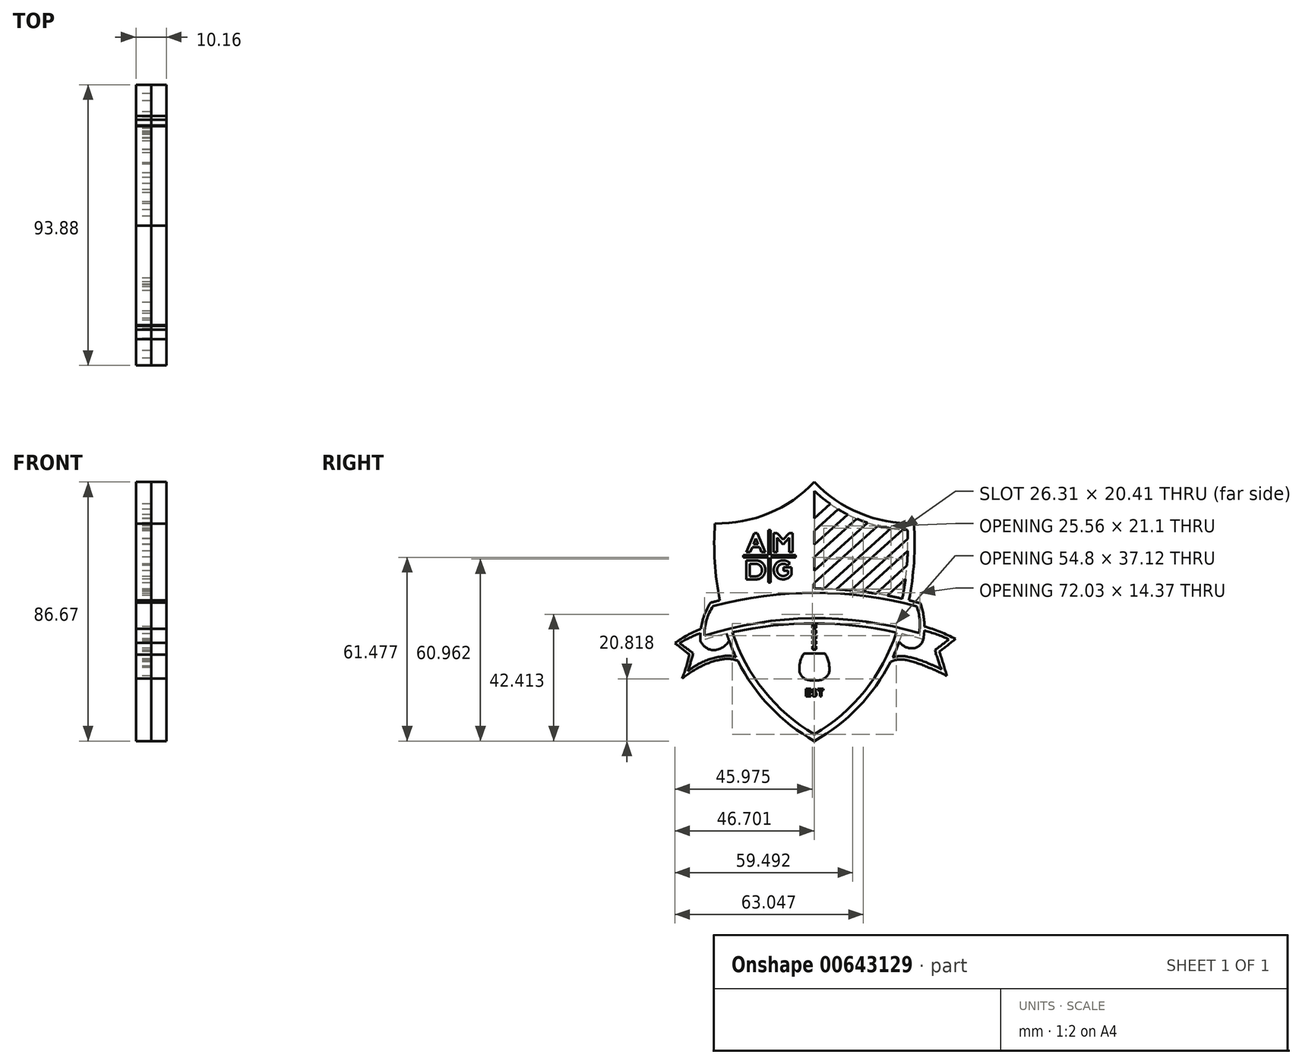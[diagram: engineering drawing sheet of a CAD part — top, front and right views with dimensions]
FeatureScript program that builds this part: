
annotation { "Feature Type Name" : "Feature", "Feature Type Description" : "" }
export const myFeature = defineFeature(function(context is Context, id is Id, definition is map)
    precondition{}
    {
        {
            var Q0;
            Q0=qCreatedBy(makeId("Right.planeOp"),FACE);
            var sketch = newSketch(context, id + "F0", { "sketchPlane" : qUnion([Q0])});
            skArc(sketch, "E0", {"start": v(35.01, -5.08) * mm, "mid": v(35.21, -0.55) * mm, "end": v(34.2, 3.87) * mm});
            skArc(sketch, "E1", {"start": v(-33.87, 3.96) * mm, "mid": v(-36.1, -0.78) * mm, "end": v(-36.75, -5.97) * mm});
            skArc(sketch, "E2", {"start": v(34.2, 3.87) * mm, "mid": v(0.17, 8.4) * mm, "end": v(-33.87, 3.96) * mm});
            skArc(sketch, "E3", {"start": v(35.01, -5.08) * mm, "mid": v(-0.93, -0.11) * mm, "end": v(-36.75, -5.97) * mm});
            skArc(sketch, "E4", {"start": v(36.42, -7.25) * mm, "mid": v(36.72, -1.13) * mm, "end": v(35.5, 4.87) * mm});
            skArc(sketch, "E5", {"start": v(-34.73, 5.08) * mm, "mid": v(-37.42, -1.04) * mm, "end": v(-38.12, -7.7) * mm});
            skArc(sketch, "E6", {"start": v(36.42, -7.25) * mm, "mid": v(-0.88, -1.82) * mm, "end": v(-38.12, -7.7) * mm});
            skArc(sketch, "E7", {"start": v(35.5, 4.87) * mm, "mid": v(0.4, 9.77) * mm, "end": v(-34.73, 5.08) * mm});
            skArc(sketch, "E8", {"start": v(42.52, -17.27) * mm, "mid": v(40.68, -16.28) * mm, "end": v(38.75, -15.48) * mm});
            skArc(sketch, "E9", {"start": v(38.75, -15.48) * mm, "mid": v(35.05, -14.03) * mm, "end": v(31.21, -13.03) * mm});
            skArc(sketch, "E10", {"start": v(44.98, -7.2) * mm, "mid": v(40.94, -5.52) * mm, "end": v(36.76, -4.21) * mm});
            skArc(sketch, "E11", {"start": v(40.3, -10.77) * mm, "mid": v(42.65, -9) * mm, "end": v(44.98, -7.2) * mm});
            skArc(sketch, "E12", {"start": v(40.3, -10.77) * mm, "mid": v(41.33, -14.05) * mm, "end": v(42.52, -17.27) * mm});
            skArc(sketch, "E13", {"start": v(31.21, -13.03) * mm, "mid": v(28.68, -12.79) * mm, "end": v(26.17, -13.23) * mm});
            skArc(sketch, "E14", {"start": v(41.76, -11.27) * mm, "mid": v(44.52, -9.2) * mm, "end": v(47.17, -7) * mm});
            skArc(sketch, "E15", {"start": v(47.17, -7) * mm, "mid": v(42.07, -4.7) * mm, "end": v(36.8, -2.83) * mm});
            skArc(sketch, "E16", {"start": v(44.3, -19.42) * mm, "mid": v(43.1, -15.33) * mm, "end": v(41.76, -11.27) * mm});
            skArc(sketch, "E17", {"start": v(30.72, -14.08) * mm, "mid": v(28.05, -13.93) * mm, "end": v(25.47, -14.65) * mm});
            skArc(sketch, "E18", {"start": v(38.1, -16.57) * mm, "mid": v(34.47, -15.16) * mm, "end": v(30.72, -14.08) * mm});
            skArc(sketch, "E19", {"start": v(44.3, -19.42) * mm, "mid": v(41.24, -17.9) * mm, "end": v(38.1, -16.57) * mm});
            skArc(sketch, "E20", {"start": v(28.41, -7.92) * mm, "mid": v(30.17, -9.57) * mm, "end": v(32.5, -10.18) * mm});
            skArc(sketch, "E21", {"start": v(-38.1, -5.07) * mm, "mid": v(-41.67, -6.6) * mm, "end": v(-45.13, -8.4) * mm});
            skArc(sketch, "E22", {"start": v(-37.95, -3.68) * mm, "mid": v(-42.47, -5.78) * mm, "end": v(-46.71, -8.4) * mm});
            skArc(sketch, "E23", {"start": v(-45.13, -8.4) * mm, "mid": v(-42.84, -10.14) * mm, "end": v(-40.5, -11.82) * mm});
            skArc(sketch, "E24", {"start": v(-46.71, -8.4) * mm, "mid": v(-44.24, -10.34) * mm, "end": v(-41.78, -12.28) * mm});
            skArc(sketch, "E25", {"start": v(-42.3, -17.82) * mm, "mid": v(-41.39, -14.83) * mm, "end": v(-40.5, -11.82) * mm});
            skArc(sketch, "E26", {"start": v(-44.22, -20.31) * mm, "mid": v(-42.88, -16.33) * mm, "end": v(-41.78, -12.28) * mm});
            skArc(sketch, "E27", {"start": v(-25.6, -14.38) * mm, "mid": v(-28.25, -13.71) * mm, "end": v(-30.97, -13.91) * mm});
            skArc(sketch, "E28", {"start": v(-26.2, -13.15) * mm, "mid": v(-28.67, -12.67) * mm, "end": v(-31.17, -12.95) * mm});
            skArc(sketch, "E29", {"start": v(-37.65, -16.1) * mm, "mid": v(-41.05, -18.02) * mm, "end": v(-44.22, -20.31) * mm});
            skArc(sketch, "E30", {"start": v(-38.7, -15.4) * mm, "mid": v(-40.56, -16.53) * mm, "end": v(-42.3, -17.82) * mm});
            skLineSegment(sketch, "E31", {"start": v(30.35, 28.58) * mm, "end": v(30.3, 28.58) * mm});
            skLineSegment(sketch, "E32", {"start": v(0, 42.48) * mm, "end": v(0, 9.77) * mm});
            skLineSegment(sketch, "E33", {"start": v(0, 33.25) * mm, "end": v(5.34, 38.07) * mm});
            skLineSegment(sketch, "E34", {"start": v(0, 29.1) * mm, "end": v(7.99, 36.33) * mm});
            skLineSegment(sketch, "E35", {"start": v(0, 24.53) * mm, "end": v(11.12, 34.58) * mm});
            skLineSegment(sketch, "E36", {"start": v(0, 20.39) * mm, "end": v(14.14, 33.17) * mm});
            skLineSegment(sketch, "E37", {"start": v(0, 11.67) * mm, "end": v(21.19, 30.83) * mm});
            skLineSegment(sketch, "E38", {"start": v(0, 15.8) * mm, "end": v(17.72, 31.83) * mm});
            skArc(sketch, "E39", {"start": v(-34.38, -10.75) * mm, "mid": v(-31, -10.03) * mm, "end": v(-28.52, -7.6) * mm});
            skArc(sketch, "E40", {"start": v(-33.27, 31.59) * mm, "mid": v(-33.3, 18.69) * mm, "end": v(-31.6, 5.9) * mm});
            skArc(sketch, "E41", {"start": v(0, 42.48) * mm, "mid": v(14.35, 33.08) * mm, "end": v(31.13, 29.48) * mm});
            skArc(sketch, "E42", {"start": v(-31.12, 29.48) * mm, "mid": v(-14.35, 33.09) * mm, "end": v(0, 42.48) * mm});
            skLineSegment(sketch, "E43", {"start": v(3.18, 9.73) * mm, "end": v(25.56, 29.96) * mm});
            skLineSegment(sketch, "E44", {"start": v(7.38, 9.56) * mm, "end": v(29.5, 29.55) * mm});
            skLineSegment(sketch, "E45", {"start": v(12.15, 9.2) * mm, "end": v(31.23, 26.45) * mm});
            skArc(sketch, "E46", {"start": v(-31.12, 29.47) * mm, "mid": v(-30.97, 17.9) * mm, "end": v(-29.4, 6.43) * mm});
            skArc(sketch, "E47", {"start": v(32.5, -10.18) * mm, "mid": v(34.96, -9.38) * mm, "end": v(36.42, -7.25) * mm});
            skArc(sketch, "E48", {"start": v(-38.12, -7.7) * mm, "mid": v(-36.6, -9.65) * mm, "end": v(-34.38, -10.75) * mm});
            skArc(sketch, "E49", {"start": v(-31.17, -12.95) * mm, "mid": v(-35.05, -13.83) * mm, "end": v(-38.7, -15.4) * mm});
            skArc(sketch, "E50", {"start": v(-30.97, -13.91) * mm, "mid": v(-34.4, -14.73) * mm, "end": v(-37.65, -16.1) * mm});
            skArc(sketch, "E51", {"start": v(-29.33, -5.25) * mm, "mid": v(-18.08, -26.01) * mm, "end": v(0, -41.2) * mm});
            skLineSegment(sketch, "E52", {"start": v(0, -41.2) * mm, "end": v(0, -38.94) * mm});
            skArc(sketch, "E53", {"start": v(0, -38.94) * mm, "mid": v(16.83, -24.43) * mm, "end": v(27.39, -4.87) * mm});
            skArc(sketch, "E54", {"start": v(0, -41.2) * mm, "mid": v(18.06, -26.04) * mm, "end": v(29.3, -5.32) * mm});
            skArc(sketch, "E55", {"start": v(-27.4, -4.81) * mm, "mid": v(-16.85, -24.4) * mm, "end": v(0, -38.94) * mm});
            skArc(sketch, "E56", {"start": v(31.6, 5.9) * mm, "mid": v(33.3, 18.68) * mm, "end": v(33.28, 31.58) * mm});
            skArc(sketch, "E57", {"start": v(29.4, 6.43) * mm, "mid": v(30.98, 17.9) * mm, "end": v(31.13, 29.48) * mm});
            skLineSegment(sketch, "E58", {"start": v(24.45, 7.47) * mm, "end": v(30.47, 12.95) * mm});
            skLineSegment(sketch, "E59", {"start": v(20.61, 8.14) * mm, "end": v(30.95, 17.52) * mm});
            skLineSegment(sketch, "E60", {"start": v(16.23, 8.76) * mm, "end": v(31.2, 22.33) * mm});
            skArc(sketch, "E61", {"start": v(0, 45.47) * mm, "mid": v(15.18, 35.03) * mm, "end": v(33.28, 31.58) * mm});
            skArc(sketch, "E62", {"start": v(-33.27, 31.59) * mm, "mid": v(-15.18, 35.03) * mm, "end": v(0, 45.47) * mm});
            skLineSegment(sketch, "E63", {"start": v(-14.62, 20.25) * mm, "end": v(-6.23, 20.25) * mm});
            skLineSegment(sketch, "E64", {"start": v(-6.23, 20.25) * mm, "end": v(-6.23, 21) * mm});
            skLineSegment(sketch, "E65", {"start": v(-6.23, 21) * mm, "end": v(-14.62, 21) * mm});
            skLineSegment(sketch, "E66", {"start": v(-14.62, 21) * mm, "end": v(-14.62, 29.4) * mm});
            skLineSegment(sketch, "E67", {"start": v(-14.62, 29.4) * mm, "end": v(-15.37, 29.4) * mm});
            skLineSegment(sketch, "E68", {"start": v(-15.37, 21) * mm, "end": v(-23.76, 21) * mm});
            skLineSegment(sketch, "E69", {"start": v(-23.76, 21) * mm, "end": v(-23.76, 20.25) * mm});
            skLineSegment(sketch, "E70", {"start": v(-15.37, 20.25) * mm, "end": v(-15.37, 11.86) * mm});
            skLineSegment(sketch, "E71", {"start": v(-15.37, 11.86) * mm, "end": v(-14.62, 11.86) * mm});
            skLineSegment(sketch, "E72", {"start": v(-14.62, 11.86) * mm, "end": v(-14.62, 20.25) * mm});
            skLineSegment(sketch, "E73", {"start": v(-19.08, 28.38) * mm, "end": v(-20.07, 28.38) * mm});
            skLineSegment(sketch, "E74", {"start": v(-20.07, 28.38) * mm, "end": v(-22.75, 22.02) * mm});
            skLineSegment(sketch, "E75", {"start": v(-15.37, 29.4) * mm, "end": v(-15.37, 21) * mm});
            skLineSegment(sketch, "E76", {"start": v(-16.4, 22.02) * mm, "end": v(-17.66, 22.02) * mm});
            skLineSegment(sketch, "E77", {"start": v(-22.75, 22.02) * mm, "end": v(-21.47, 22.02) * mm});
            skLineSegment(sketch, "E78", {"start": v(-20.34, 24.7) * mm, "end": v(-18.79, 24.7) * mm});
            skLineSegment(sketch, "E79", {"start": v(-18.79, 24.7) * mm, "end": v(-19.57, 26.54) * mm});
            skLineSegment(sketch, "E80", {"start": v(-20.34, 24.7) * mm, "end": v(-19.57, 26.54) * mm});
            skLineSegment(sketch, "E81", {"start": v(-20.77, 23.67) * mm, "end": v(-21.47, 22.02) * mm});
            skLineSegment(sketch, "E82", {"start": v(-20.77, 23.67) * mm, "end": v(-18.36, 23.67) * mm});
            skLineSegment(sketch, "E83", {"start": v(-18.36, 23.67) * mm, "end": v(-17.66, 22.02) * mm});
            skLineSegment(sketch, "E84", {"start": v(-12.46, 22.02) * mm, "end": v(-12.46, 26.83) * mm});
            skLineSegment(sketch, "E85", {"start": v(-7.25, 22.02) * mm, "end": v(-8.4, 22.02) * mm});
            skLineSegment(sketch, "E86", {"start": v(-8.4, 22.02) * mm, "end": v(-8.4, 26.83) * mm});
            skLineSegment(sketch, "E87", {"start": v(-12.46, 26.83) * mm, "end": v(-10.43, 24.54) * mm});
            skLineSegment(sketch, "E88", {"start": v(-10.43, 24.54) * mm, "end": v(-8.4, 26.83) * mm});
            skLineSegment(sketch, "E89", {"start": v(-7.25, 28.38) * mm, "end": v(-7.25, 22.02) * mm});
            skLineSegment(sketch, "E90", {"start": v(-12.46, 22.02) * mm, "end": v(-13.6, 22.02) * mm});
            skLineSegment(sketch, "E91", {"start": v(-13.6, 28.38) * mm, "end": v(-13.6, 22.02) * mm});
            skLineSegment(sketch, "E92", {"start": v(-19.08, 28.38) * mm, "end": v(-16.4, 22.02) * mm});
            skLineSegment(sketch, "E93", {"start": v(-7.25, 28.38) * mm, "end": v(-8.4, 28.38) * mm});
            skLineSegment(sketch, "E94", {"start": v(-8.4, 28.38) * mm, "end": v(-10.43, 26.17) * mm});
            skLineSegment(sketch, "E95", {"start": v(-13.6, 28.38) * mm, "end": v(-12.46, 28.38) * mm});
            skLineSegment(sketch, "E96", {"start": v(-12.46, 28.38) * mm, "end": v(-10.43, 26.17) * mm});
            skLineSegment(sketch, "E97", {"start": v(-22.75, 19.22) * mm, "end": v(-22.75, 12.87) * mm});
            skLineSegment(sketch, "E98", {"start": v(-21.61, 13.9) * mm, "end": v(-21.61, 18.07) * mm});
            skLineSegment(sketch, "E99", {"start": v(-21.61, 18.07) * mm, "end": v(-19.7, 18.07) * mm});
            skLineSegment(sketch, "E100", {"start": v(-21.61, 13.9) * mm, "end": v(-19.72, 13.9) * mm});
            skArc(sketch, "E101", {"start": v(-19.59, 12.87) * mm, "mid": v(-16.38, 16.05) * mm, "end": v(-19.59, 19.22) * mm});
            skArc(sketch, "E102", {"start": v(-19.72, 13.9) * mm, "mid": v(-17.53, 15.97) * mm, "end": v(-19.7, 18.07) * mm});
            skLineSegment(sketch, "E103", {"start": v(-19.59, 19.22) * mm, "end": v(-22.75, 19.22) * mm});
            skLineSegment(sketch, "E104", {"start": v(-19.59, 12.87) * mm, "end": v(-22.75, 12.87) * mm});
            skLineSegment(sketch, "E105", {"start": v(-23.76, 20.25) * mm, "end": v(-15.37, 20.25) * mm});
            skArc(sketch, "E106", {"start": v(-10.43, 19.24) * mm, "mid": v(-12.68, 18.3) * mm, "end": v(-13.6, 16.06) * mm});
            skArc(sketch, "E107", {"start": v(-13.6, 16.06) * mm, "mid": v(-12.68, 13.81) * mm, "end": v(-10.43, 12.88) * mm});
            skArc(sketch, "E108", {"start": v(-10.43, 18.1) * mm, "mid": v(-11.87, 17.5) * mm, "end": v(-12.46, 16.06) * mm});
            skArc(sketch, "E109", {"start": v(-12.46, 16.06) * mm, "mid": v(-11.87, 14.61) * mm, "end": v(-10.43, 14.02) * mm});
            skLineSegment(sketch, "E110", {"start": v(-9, 17.5) * mm, "end": v(-8.19, 18.3) * mm});
            skArc(sketch, "E111", {"start": v(-9, 17.5) * mm, "mid": v(-9.65, 17.95) * mm, "end": v(-10.43, 18.1) * mm});
            skArc(sketch, "E112", {"start": v(-8.19, 18.3) * mm, "mid": v(-9.22, 19) * mm, "end": v(-10.43, 19.24) * mm});
            skLineSegment(sketch, "E113", {"start": v(-10.34, 16.94) * mm, "end": v(-7.63, 16.94) * mm});
            skLineSegment(sketch, "E114", {"start": v(-10.34, 16.94) * mm, "end": v(-10.34, 15.8) * mm});
            skLineSegment(sketch, "E115", {"start": v(-10.34, 15.8) * mm, "end": v(-8.77, 15.8) * mm});
            skArc(sketch, "E116", {"start": v(-10.43, 12.88) * mm, "mid": v(-8.86, 13.3) * mm, "end": v(-7.7, 14.44) * mm});
            skArc(sketch, "E117", {"start": v(-7.7, 14.44) * mm, "mid": v(-7.65, 14.54) * mm, "end": v(-7.63, 14.66) * mm});
            skArc(sketch, "E118", {"start": v(-10.43, 14.02) * mm, "mid": v(-9.56, 14.22) * mm, "end": v(-8.85, 14.77) * mm});
            skArc(sketch, "E119", {"start": v(-8.85, 14.77) * mm, "mid": v(-8.8, 14.86) * mm, "end": v(-8.77, 14.96) * mm});
            skLineSegment(sketch, "E120", {"start": v(-8.77, 14.96) * mm, "end": v(-8.77, 15.8) * mm});
            skLineSegment(sketch, "E121", {"start": v(-7.63, 16.94) * mm, "end": v(-7.63, 14.66) * mm});
            skSolve(sketch);
        }
        {
            var Q0;
            Q0 = qSketchRegion(id + "F0", true);
            var Q1;
            {var subQ0=sQuery(id+"F0.wireOp",EDGE,"E33");Q1=makeQuery(id+"F0.imprint","IMPRINT",FACE,{"disambiguationData":[TD([[makeQuery(id+"F0.imprint","IMPRINT",EDGE,{"derivedFrom":subQ0}),-1.0]])]});}
            var Q2;
            {var subQ0=sQuery(id+"F0.wireOp",EDGE,"E35");Q2=makeQuery(id+"F0.imprint","IMPRINT",FACE,{"disambiguationData":[TD([[makeQuery(id+"F0.imprint","IMPRINT",EDGE,{"derivedFrom":subQ0}),-1.0]])]});}
            var Q3;
            {var subQ0=sQuery(id+"F0.wireOp",EDGE,"E37");Q3=makeQuery(id+"F0.imprint","IMPRINT",FACE,{"disambiguationData":[TD([[makeQuery(id+"F0.imprint","IMPRINT",EDGE,{"derivedFrom":subQ0}),1.0]])]});}
            var Q4;
            {var subQ0=sQuery(id+"F0.wireOp",EDGE,"O8f0gSgc-beU1-EBJn-roK9-9nWLyk56kTGw");Q4=makeQuery(id+"F0.imprint","IMPRINT",FACE,{"disambiguationData":[TD([[makeQuery(id+"F0.imprint","IMPRINT",EDGE,{"derivedFrom":subQ0}),-1.0]])]});}
            var Q5;
            {var subQ0=sQuery(id+"F0.wireOp",EDGE,"kELnW45c-3cLN-zG9Y-0OCP-nixKJG5hk9dS");Q5=makeQuery(id+"F0.imprint","IMPRINT",FACE,{"disambiguationData":[TD([[makeQuery(id+"F0.imprint","IMPRINT",EDGE,{"derivedFrom":subQ0}),-1.0]])]});}
            var Q6;
            {var subQ0=sQuery(id+"F0.wireOp",EDGE,"aP0UoHQW-60sD-qkYz-xB7F-yd6cjnAi5jye");Q6=makeQuery(id+"F0.imprint","IMPRINT",FACE,{"disambiguationData":[TD([[makeQuery(id+"F0.imprint","IMPRINT",EDGE,{"derivedFrom":subQ0}),-1.0]])]});}
            var Q7;
            Q7=makeQuery(id+"F0.imprint","IMPRINT",FACE,{"disambiguationData":[TD([[makeQuery(id+"F0.imprint","IMPRINT",EDGE,{"derivedFrom":sQuery(id+"F0.wireOp",EDGE,"TzDbxLRU-RwqV-JGS8-R2m0-YrzYSDwwyyDc")}),1.0]])]});
            var Q8;
            Q8=makeQuery(id+"F0.imprint","IMPRINT",FACE,{"disambiguationData":[TD([[makeQuery(id+"F0.imprint","IMPRINT",EDGE,{"derivedFrom":sQuery(id+"F0.wireOp",EDGE,"NQOFpSlj-IhlP-Osex-fz3N-qHAzP8grofBZ")}),-1.0]])]});
            var Q9;
            {var subQ3=sQuery(id+"F0.wireOp",EDGE,"E20");Q9=makeQuery(id+"F0.imprint","IMPRINT",FACE,{"disambiguationData":[TD([[makeQuery(id+"F0.imprint","IMPRINT",EDGE,{"derivedFrom":subQ3}),1.0]])]});}
            var Q10;
            {var subQ4=sQuery(id+"F0.wireOp",EDGE,"gYNnnUih-wfO3-EVgg-BHTK-YfAPz8Tz6hfM");Q10=makeQuery(id+"F0.imprint","IMPRINT",FACE,{"disambiguationData":[TD([[makeQuery(id+"F0.imprint","IMPRINT",EDGE,{"derivedFrom":subQ4}),1.0]])]});}
            var Q11;
            {var subQ5=sQuery(id+"F0.wireOp",EDGE,"X1GVdF0t-RVGf-viMC-tvin-t861eVOr0CtA");Q11=makeQuery(id+"F0.imprint","IMPRINT",FACE,{"disambiguationData":[TD([[makeQuery(id+"F0.imprint","IMPRINT",EDGE,{"derivedFrom":subQ5}),-1.0]])]});}
            var Q12;
            {var subQ0=sQuery(id+"F0.wireOp",EDGE,"E43");Q12=makeQuery(id+"F0.imprint","IMPRINT",FACE,{"disambiguationData":[TD([[makeQuery(id+"F0.imprint","IMPRINT",EDGE,{"derivedFrom":subQ0}),-1.0]])]});}
            var Q13;
            {var subQ0=sQuery(id+"F0.wireOp",EDGE,"E45");Q13=makeQuery(id+"F0.imprint","IMPRINT",FACE,{"disambiguationData":[TD([[makeQuery(id+"F0.imprint","IMPRINT",EDGE,{"derivedFrom":subQ0}),-1.0]])]});}
            var Q14;
            {var subQ0=sQuery(id+"F0.wireOp",EDGE,"rI9aA2D5-3RCz-biGW-fjSb-nJGNOB4AB7o3");Q14=makeQuery(id+"F0.imprint","IMPRINT",FACE,{"disambiguationData":[TD([[makeQuery(id+"F0.imprint","IMPRINT",EDGE,{"derivedFrom":subQ0}),-1.0]])]});}
            var Q15;
            Q15=makeQuery(id+"F0.imprint","IMPRINT",FACE,{"disambiguationData":[TD([[makeQuery(id+"F0.imprint","IMPRINT",EDGE,{"derivedFrom":sQuery(id+"F0.wireOp",EDGE,"7KTSsoSh-OWG0-qBIn-ycyS-VPeFdv1TA5E4")}),1.0]])]});
            var Q16;
            Q16=makeQuery(id+"F0.imprint","IMPRINT",FACE,{"disambiguationData":[TD([[makeQuery(id+"F0.imprint","IMPRINT",EDGE,{"derivedFrom":sQuery(id+"F0.wireOp",EDGE,"oL9Hh9FE-Zn1f-5m7H-AjiJ-lgKje7s23mEt")}),1.0]])]});
            var Q17;
            {var subQ4=sQuery(id+"F0.wireOp",EDGE,"E39");Q17=makeQuery(id+"F0.imprint","IMPRINT",FACE,{"disambiguationData":[TD([[makeQuery(id+"F0.imprint","IMPRINT",EDGE,{"derivedFrom":subQ4}),1.0]])]});}
            var Q18;
            {var subQ0=sQuery(id+"F0.wireOp",EDGE,"E58");Q18=makeQuery(id+"F0.imprint","IMPRINT",FACE,{"disambiguationData":[TD([[makeQuery(id+"F0.imprint","IMPRINT",EDGE,{"derivedFrom":subQ0}),1.0]])]});}
            var Q19;
            Q19=makeQuery(id+"F0.imprint","IMPRINT",FACE,{"disambiguationData":[TD([[makeQuery(id+"F0.imprint","IMPRINT",EDGE,{"derivedFrom":sQuery(id+"F0.wireOp",EDGE,"0lDTRp4B-xh9S-EdmV-e4qE-ALoVxaatGYrM")}),-1.0]])]});
            var Q20;
            Q20=makeQuery(id+"F0.imprint","IMPRINT",FACE,{"disambiguationData":[TD([[makeQuery(id+"F0.imprint","IMPRINT",EDGE,{"derivedFrom":sQuery(id+"F0.wireOp",EDGE,"E78")}),1.0]])]});
            var Q21;
            Q21=makeQuery(id+"F0.imprint","IMPRINT",FACE,{"disambiguationData":[TD([[makeQuery(id+"F0.imprint","IMPRINT",EDGE,{"derivedFrom":sQuery(id+"F0.wireOp",EDGE,"E98")}),-1.0]])]});
            extrude(context, id + "F1", {"entities" : qUnion([Q0, Q1, Q2, Q3, Q4, Q5, Q6, Q7, Q8, Q9, Q10, Q11, Q12, Q13, Q14, Q15, Q16, Q17, Q18, Q19, Q20, Q21]), "depth" : 10.16 * mm, "offsetDistance" : 25.4 * mm});
        }
        {
            var Q0;
            Q0 = qSketchRegion(id + "F0", true);
            var Q1;
            Q1=makeQuery(id+"F0.imprint","IMPRINT",FACE,{"disambiguationData":[TD([[makeQuery(id+"F0.imprint","IMPRINT",EDGE,{"derivedFrom":sQuery(id+"F0.wireOp",EDGE,"E0")}),1.0]])]});
            var Q2;
            {var subQ0=sQuery(id+"F0.wireOp",EDGE,"E37");Q2=makeQuery(id+"F0.imprint","IMPRINT",FACE,{"disambiguationData":[TD([[makeQuery(id+"F0.imprint","IMPRINT",EDGE,{"derivedFrom":subQ0}),-1.0]])]});}
            var Q3;
            {var subQ0=sQuery(id+"F0.wireOp",EDGE,"E36");Q3=makeQuery(id+"F0.imprint","IMPRINT",FACE,{"disambiguationData":[TD([[makeQuery(id+"F0.imprint","IMPRINT",EDGE,{"derivedFrom":subQ0}),-1.0]])]});}
            var Q4;
            {var subQ0=sQuery(id+"F0.wireOp",EDGE,"IQEnVNMN-KRev-ARMe-WBoh-NiKV1olaI5Jl");Q4=makeQuery(id+"F0.imprint","IMPRINT",FACE,{"disambiguationData":[TD([[makeQuery(id+"F0.imprint","IMPRINT",EDGE,{"derivedFrom":subQ0}),-1.0]])]});}
            var Q5;
            {var subQ0=sQuery(id+"F0.wireOp",EDGE,"LgnPcSxb-k7K1-XdEU-6XJT-hcyGKBAHDmjx");Q5=makeQuery(id+"F0.imprint","IMPRINT",FACE,{"disambiguationData":[TD([[makeQuery(id+"F0.imprint","IMPRINT",EDGE,{"derivedFrom":subQ0}),-1.0]])]});}
            var Q6;
            {var subQ3=sQuery(id+"F0.wireOp",EDGE,"TRkPiesn-OKkT-UC3K-NN5B-XfNRiC2bw1Lp");Q6=makeQuery(id+"F0.imprint","IMPRINT",FACE,{"disambiguationData":[TD([[makeQuery(id+"F0.imprint","IMPRINT",EDGE,{"derivedFrom":subQ3}),-1.0]])]});}
            var Q7;
            {var subQ0=sQuery(id+"F0.wireOp",EDGE,"E34");Q7=makeQuery(id+"F0.imprint","IMPRINT",FACE,{"disambiguationData":[TD([[makeQuery(id+"F0.imprint","IMPRINT",EDGE,{"derivedFrom":subQ0}),-1.0]])]});}
            var Q8;
            {var subQ3=sQuery(id+"F0.wireOp",EDGE,"E33");Q8=makeQuery(id+"F0.imprint","IMPRINT",FACE,{"disambiguationData":[TD([[makeQuery(id+"F0.imprint","IMPRINT",EDGE,{"derivedFrom":subQ3}),1.0]])]});}
            var Q9;
            {var subQ0=sQuery(id+"F0.wireOp",EDGE,"E21");Q9=makeQuery(id+"F0.imprint","IMPRINT",FACE,{"disambiguationData":[TD([[makeQuery(id+"F0.imprint","IMPRINT",EDGE,{"derivedFrom":subQ0}),1.0]])]});}
            var Q10;
            {var subQ0=sQuery(id+"F0.wireOp",EDGE,"u2aVZmCq-nqS6-VN9p-M0An-2YUbfrqEEw19");Q10=makeQuery(id+"F0.imprint","IMPRINT",FACE,{"disambiguationData":[TD([[makeQuery(id+"F0.imprint","IMPRINT",EDGE,{"derivedFrom":subQ0}),-1.0]])]});}
            var Q11;
            Q11=makeQuery(id+"F0.imprint","IMPRINT",FACE,{"disambiguationData":[TD([[makeQuery(id+"F0.imprint","IMPRINT",EDGE,{"derivedFrom":sQuery(id+"F0.wireOp",EDGE,"E8")}),-1.0]])]});
            var Q12;
            Q12=makeQuery(id+"F0.imprint","IMPRINT",FACE,{"disambiguationData":[TD([[makeQuery(id+"F0.imprint","IMPRINT",EDGE,{"derivedFrom":sQuery(id+"F0.wireOp",EDGE,"ynKPf5w3-M3kH-zNFM-uhaN-6HMNebFdzvny")}),-1.0]])]});
            var Q13;
            Q13=makeQuery(id+"F0.imprint","IMPRINT",FACE,{"disambiguationData":[TD([[makeQuery(id+"F0.imprint","IMPRINT",EDGE,{"derivedFrom":sQuery(id+"F0.wireOp",EDGE,"AmkVrQGs-azwW-AMP0-fGoQ-Nt3R7YTiKGt6")}),-1.0]])]});
            var Q14;
            Q14=makeQuery(id+"F0.imprint","IMPRINT",FACE,{"disambiguationData":[TD([[makeQuery(id+"F0.imprint","IMPRINT",EDGE,{"derivedFrom":sQuery(id+"F0.wireOp",EDGE,"7KTSsoSh-OWG0-qBIn-ycyS-VPeFdv1TA5E4")}),-1.0]])]});
            var Q15;
            Q15=makeQuery(id+"F0.imprint","IMPRINT",FACE,{"disambiguationData":[TD([[makeQuery(id+"F0.imprint","IMPRINT",EDGE,{"derivedFrom":sQuery(id+"F0.wireOp",EDGE,"oZxUZDlT-5PEi-zmkT-ZY6j-ThAwYOyqQCs4")}),1.0]])]});
            var Q16;
            Q16=makeQuery(id+"F0.imprint","IMPRINT",FACE,{"disambiguationData":[TD([[makeQuery(id+"F0.imprint","IMPRINT",EDGE,{"derivedFrom":sQuery(id+"F0.wireOp",EDGE,"Pujzfh8l-lzfB-vfAf-br6m-x0UQDaA8CgJr")}),-1.0]])]});
            var Q17;
            {var subQ0=sQuery(id+"F0.wireOp",EDGE,"u2aVZmCq-nqS6-VN9p-M0An-2YUbfrqEEw19");Q17=makeQuery(id+"F0.imprint","IMPRINT",FACE,{"disambiguationData":[TD([[makeQuery(id+"F0.imprint","IMPRINT",EDGE,{"derivedFrom":subQ0}),1.0]])]});}
            var Q18;
            {var subQ0=sQuery(id+"F0.wireOp",EDGE,"gmcIIbZD-PCMP-5Jrr-N2pD-fV7yzqhyJVgi");Q18=makeQuery(id+"F0.imprint","IMPRINT",FACE,{"disambiguationData":[TD([[makeQuery(id+"F0.imprint","IMPRINT",EDGE,{"derivedFrom":subQ0}),1.0]])]});}
            var Q19;
            {var subQ0=sQuery(id+"F0.wireOp",EDGE,"E44");Q19=makeQuery(id+"F0.imprint","IMPRINT",FACE,{"disambiguationData":[TD([[makeQuery(id+"F0.imprint","IMPRINT",EDGE,{"derivedFrom":subQ0}),-1.0]])]});}
            var Q20;
            {var subQ3=sQuery(id+"F0.wireOp",EDGE,"p52YEaph-7iA0-zj5O-URsX-pYWkMtOm4PNA");Q20=makeQuery(id+"F0.imprint","IMPRINT",FACE,{"disambiguationData":[TD([[makeQuery(id+"F0.imprint","IMPRINT",EDGE,{"derivedFrom":subQ3}),-1.0]])]});}
            var Q21;
            Q21=makeQuery(id+"F0.imprint","IMPRINT",FACE,{"disambiguationData":[TD([[makeQuery(id+"F0.imprint","IMPRINT",EDGE,{"derivedFrom":sQuery(id+"F0.wireOp",EDGE,"MvKlj1QA-cJ2O-iLoF-NrKP-IF7acZl89Xwh")}),-1.0]])]});
            var Q22;
            Q22=makeQuery(id+"F0.imprint","IMPRINT",FACE,{"disambiguationData":[TD([[makeQuery(id+"F0.imprint","IMPRINT",EDGE,{"derivedFrom":sQuery(id+"F0.wireOp",EDGE,"31fmbc6z-1vKk-B0Yj-qSTF-2MqDuvIRsLE5")}),1.0]])]});
            var Q23;
            Q23=makeQuery(id+"F0.imprint","IMPRINT",FACE,{"disambiguationData":[TD([[makeQuery(id+"F0.imprint","IMPRINT",EDGE,{"derivedFrom":sQuery(id+"F0.wireOp",EDGE,"8K0aIbxq-i1XX-BUkf-RSue-FuYtuOvytJvJ")}),1.0]])]});
            var Q24;
            {var subQ0=sQuery(id+"F0.wireOp",EDGE,"E59");Q24=makeQuery(id+"F0.imprint","IMPRINT",FACE,{"disambiguationData":[TD([[makeQuery(id+"F0.imprint","IMPRINT",EDGE,{"derivedFrom":subQ0}),1.0]])]});}
            var Q25;
            {var subQ3=sQuery(id+"F0.wireOp",EDGE,"E58");Q25=makeQuery(id+"F0.imprint","IMPRINT",FACE,{"disambiguationData":[TD([[makeQuery(id+"F0.imprint","IMPRINT",EDGE,{"derivedFrom":subQ3}),-1.0]])]});}
            var Q26;
            {var subQ0=sQuery(id+"F0.wireOp",EDGE,"E53");Q26=makeQuery(id+"F0.imprint","IMPRINT",FACE,{"disambiguationData":[TD([[makeQuery(id+"F0.imprint","IMPRINT",EDGE,{"derivedFrom":subQ0}),1.0]])]});}
            var Q27;
            Q27=makeQuery(id+"F0.imprint","IMPRINT",FACE,{"disambiguationData":[TD([[makeQuery(id+"F0.imprint","IMPRINT",EDGE,{"derivedFrom":sQuery(id+"F0.wireOp",EDGE,"qZWrnHlQ-psQv-lP55-t3DE-fNkFvwuKKvoo")}),1.0]])]});
            var Q28;
            Q28=makeQuery(id+"F0.imprint","IMPRINT",FACE,{"disambiguationData":[TD([[makeQuery(id+"F0.imprint","IMPRINT",EDGE,{"derivedFrom":sQuery(id+"F0.wireOp",EDGE,"E73")}),1.0]])]});
            var Q29;
            Q29=makeQuery(id+"F0.imprint","IMPRINT",FACE,{"disambiguationData":[TD([[makeQuery(id+"F0.imprint","IMPRINT",EDGE,{"derivedFrom":sQuery(id+"F0.wireOp",EDGE,"E97")}),1.0]])]});
            var Q30;
            Q30=makeQuery(id+"F0.imprint","IMPRINT",FACE,{"disambiguationData":[TD([[makeQuery(id+"F0.imprint","IMPRINT",EDGE,{"derivedFrom":sQuery(id+"F0.wireOp",EDGE,"E106")}),1.0]])]});
            var Q31;
            Q31=makeQuery(id+"F0.imprint","IMPRINT",FACE,{"disambiguationData":[TD([[makeQuery(id+"F0.imprint","IMPRINT",EDGE,{"derivedFrom":sQuery(id+"F0.wireOp",EDGE,"E84")}),1.0]])]});
            var Q32;
            Q32=makeQuery(id+"F0.imprint","IMPRINT",FACE,{"disambiguationData":[TD([[makeQuery(id+"F0.imprint","IMPRINT",EDGE,{"derivedFrom":sQuery(id+"F0.wireOp",EDGE,"E63")}),1.0]])]});
            extrude(context, id + "F2", {"entities" : qUnion([Q0, Q1, Q2, Q3, Q4, Q5, Q6, Q7, Q8, Q9, Q10, Q11, Q12, Q13, Q14, Q15, Q16, Q17, Q18, Q19, Q20, Q21, Q22, Q23, Q24, Q25, Q26, Q27, Q28, Q29, Q30, Q31, Q32]), "depth" : 5.08 * mm, "offsetDistance" : 25.4 * mm});
        }
        {
            var Q0;
            Q0=qCreatedBy(makeId("Right.planeOp"),FACE);
            var sketch = newSketch(context, id + "F3", { "sketchPlane" : qUnion([Q0])});
            skArc(sketch, "E122", {"start": v(-1.91, -20.83) * mm, "mid": v(0.05, -20.97) * mm, "end": v(2, -20.8) * mm});
            skArc(sketch, "E123", {"start": v(2, -20.8) * mm, "mid": v(3.85, -19.87) * mm, "end": v(4.95, -18.11) * mm});
            skArc(sketch, "E124", {"start": v(-4.95, -18.11) * mm, "mid": v(-3.81, -19.9) * mm, "end": v(-1.91, -20.83) * mm});
            skArc(sketch, "E125", {"start": v(-3.52, -11.89) * mm, "mid": v(-4.78, -14.87) * mm, "end": v(-4.95, -18.11) * mm});
            skArc(sketch, "E126", {"start": v(4.95, -18.11) * mm, "mid": v(4.78, -14.87) * mm, "end": v(3.52, -11.89) * mm});
            skLineSegment(sketch, "E127", {"start": v(-3.52, -11.89) * mm, "end": v(0, -11.89) * mm});
            skLineSegment(sketch, "E128", {"start": v(0, -11.89) * mm, "end": v(3.52, -11.89) * mm});
            skLineSegment(sketch, "E129", {"start": v(0, -1.95) * mm, "end": v(0.9, -2.84) * mm});
            skLineSegment(sketch, "E130", {"start": v(-0.9, -2.84) * mm, "end": v(0, -1.95) * mm});
            skLineSegment(sketch, "E131", {"start": v(-0.9, -2.84) * mm, "end": v(0, -3.73) * mm});
            skLineSegment(sketch, "E132", {"start": v(0, -3.73) * mm, "end": v(0.9, -2.84) * mm});
            skLineSegment(sketch, "E133", {"start": v(0, -3.73) * mm, "end": v(-0.9, -4.62) * mm});
            skLineSegment(sketch, "E134", {"start": v(-0.9, -4.62) * mm, "end": v(0, -5.52) * mm});
            skLineSegment(sketch, "E135", {"start": v(0, -3.73) * mm, "end": v(0.9, -4.62) * mm});
            skLineSegment(sketch, "E136", {"start": v(0.9, -4.62) * mm, "end": v(0, -5.52) * mm});
            skLineSegment(sketch, "E137", {"start": v(0, -5.52) * mm, "end": v(-0.9, -6.4) * mm});
            skLineSegment(sketch, "E138", {"start": v(0, -5.52) * mm, "end": v(0.9, -6.4) * mm});
            skLineSegment(sketch, "E139", {"start": v(0.9, -6.4) * mm, "end": v(0, -7.3) * mm});
            skLineSegment(sketch, "E140", {"start": v(0, -7.3) * mm, "end": v(-0.9, -6.4) * mm});
            skLineSegment(sketch, "E141", {"start": v(0, -7.3) * mm, "end": v(0.9, -8.2) * mm});
            skLineSegment(sketch, "E142", {"start": v(0, -7.3) * mm, "end": v(-0.9, -8.2) * mm});
            skLineSegment(sketch, "E143", {"start": v(-0.9, -8.2) * mm, "end": v(0, -9.09) * mm});
            skLineSegment(sketch, "E144", {"start": v(0.9, -8.2) * mm, "end": v(0, -9.09) * mm});
            skLineSegment(sketch, "E145", {"start": v(0.9, -9.98) * mm, "end": v(0, -9.09) * mm});
            skLineSegment(sketch, "E146", {"start": v(-0.9, -9.98) * mm, "end": v(0, -10.87) * mm});
            skLineSegment(sketch, "E147", {"start": v(0.9, -9.98) * mm, "end": v(0, -10.87) * mm});
            skLineSegment(sketch, "E148", {"start": v(-0.9, -9.98) * mm, "end": v(0, -9.09) * mm});
            skLineSegment(sketch, "E149", {"start": v(0, -9.55) * mm, "end": v(-0.45, -10) * mm});
            skLineSegment(sketch, "E150", {"start": v(0, -9.55) * mm, "end": v(0.45, -10) * mm});
            skLineSegment(sketch, "E151", {"start": v(0.45, -10) * mm, "end": v(0, -10.45) * mm});
            skLineSegment(sketch, "E152", {"start": v(0, -10.45) * mm, "end": v(-0.45, -10) * mm});
            skLineSegment(sketch, "E153", {"start": v(0, -8.66) * mm, "end": v(0.45, -8.2) * mm});
            skLineSegment(sketch, "E154", {"start": v(0.45, -8.2) * mm, "end": v(0, -7.76) * mm});
            skLineSegment(sketch, "E155", {"start": v(0, -7.76) * mm, "end": v(-0.45, -8.2) * mm});
            skLineSegment(sketch, "E156", {"start": v(-0.45, -8.2) * mm, "end": v(0, -8.66) * mm});
            skLineSegment(sketch, "E157", {"start": v(0, -5.97) * mm, "end": v(-0.45, -6.42) * mm});
            skLineSegment(sketch, "E158", {"start": v(-0.45, -6.42) * mm, "end": v(0, -6.87) * mm});
            skLineSegment(sketch, "E159", {"start": v(0, -6.87) * mm, "end": v(0.45, -6.42) * mm});
            skLineSegment(sketch, "E160", {"start": v(0.45, -6.42) * mm, "end": v(0, -5.97) * mm});
            skLineSegment(sketch, "E161", {"start": v(0, -5.08) * mm, "end": v(0.45, -4.63) * mm});
            skLineSegment(sketch, "E162", {"start": v(0.45, -4.63) * mm, "end": v(0, -4.18) * mm});
            skLineSegment(sketch, "E163", {"start": v(0, -4.18) * mm, "end": v(-0.45, -4.63) * mm});
            skLineSegment(sketch, "E164", {"start": v(-0.45, -4.63) * mm, "end": v(0, -5.08) * mm});
            skLineSegment(sketch, "E165", {"start": v(0, -2.38) * mm, "end": v(0.45, -2.83) * mm});
            skLineSegment(sketch, "E166", {"start": v(0.45, -2.83) * mm, "end": v(0, -3.28) * mm});
            skLineSegment(sketch, "E167", {"start": v(-0.45, -2.83) * mm, "end": v(0, -3.28) * mm});
            skLineSegment(sketch, "E168", {"start": v(-0.45, -2.83) * mm, "end": v(0, -2.38) * mm});
            skLineSegment(sketch, "E169", {"start": v(0, -26.31) * mm, "end": v(0, -27.97) * mm});
            skLineSegment(sketch, "E170", {"start": v(0, -27.97) * mm, "end": v(0, -32.16) * mm});
            skLineSegment(sketch, "E171", {"start": v(0, -32.16) * mm, "end": v(5.89, -32.16) * mm});
            skLineSegment(sketch, "E172", {"start": v(5.89, -32.16) * mm, "end": v(5.89, -27.97) * mm});
            skLineSegment(sketch, "E173", {"start": v(5.89, -27.97) * mm, "end": v(0, -27.97) * mm});
            skLineSegment(sketch, "E174", {"start": v(0, -27.97) * mm, "end": v(-5.89, -27.97) * mm});
            skLineSegment(sketch, "E175", {"start": v(-5.89, -27.97) * mm, "end": v(-5.89, -32.16) * mm});
            skLineSegment(sketch, "E176", {"start": v(-5.89, -32.16) * mm, "end": v(0, -32.16) * mm});
            skArc(sketch, "E177", {"start": v(0, -23.79) * mm, "mid": v(-0.75, -24.54) * mm, "end": v(0, -25.3) * mm});
            skArc(sketch, "E178", {"start": v(0, -26.31) * mm, "mid": v(0.76, -25.55) * mm, "end": v(0, -24.8) * mm});
            skArc(sketch, "E179", {"start": v(0, -25.81) * mm, "mid": v(0.26, -25.55) * mm, "end": v(0, -25.3) * mm});
            skArc(sketch, "E180", {"start": v(0, -24.29) * mm, "mid": v(-0.26, -24.54) * mm, "end": v(0, -24.8) * mm});
            skArc(sketch, "E181", {"start": v(0.18, -24.36) * mm, "mid": v(0.1, -24.3) * mm, "end": v(0, -24.29) * mm});
            skArc(sketch, "E182", {"start": v(0.53, -24) * mm, "mid": v(0.28, -23.84) * mm, "end": v(0, -23.79) * mm});
            skLineSegment(sketch, "E183", {"start": v(-0.24, -25.66) * mm, "end": v(-0.7, -25.83) * mm});
            skLineSegment(sketch, "E184", {"start": v(0.23, -24.42) * mm, "end": v(0.7, -24.25) * mm});
            skArc(sketch, "E185", {"start": v(0.7, -24.25) * mm, "mid": v(0.62, -24.12) * mm, "end": v(0.53, -24) * mm});
            skArc(sketch, "E186", {"start": v(0.23, -24.42) * mm, "mid": v(0.2, -24.39) * mm, "end": v(0.18, -24.36) * mm});
            skArc(sketch, "E187", {"start": v(-0.24, -25.66) * mm, "mid": v(-0.14, -25.77) * mm, "end": v(0, -25.81) * mm});
            skArc(sketch, "E188", {"start": v(-0.7, -25.83) * mm, "mid": v(-0.63, -25.97) * mm, "end": v(-0.54, -26.08) * mm});
            skArc(sketch, "E189", {"start": v(-0.54, -26.08) * mm, "mid": v(-0.3, -26.25) * mm, "end": v(0, -26.31) * mm});
            skLineSegment(sketch, "E190", {"start": v(1.13, -24.28) * mm, "end": v(1.13, -23.77) * mm});
            skLineSegment(sketch, "E191", {"start": v(1.13, -23.77) * mm, "end": v(3.03, -23.77) * mm});
            skLineSegment(sketch, "E192", {"start": v(3.03, -23.77) * mm, "end": v(3.03, -24.28) * mm});
            skLineSegment(sketch, "E193", {"start": v(2.33, -24.28) * mm, "end": v(3.03, -24.28) * mm});
            skLineSegment(sketch, "E194", {"start": v(1.83, -24.28) * mm, "end": v(1.13, -24.28) * mm});
            skLineSegment(sketch, "E195", {"start": v(1.83, -24.28) * mm, "end": v(1.83, -26.31) * mm});
            skLineSegment(sketch, "E196", {"start": v(1.83, -26.31) * mm, "end": v(2.33, -26.31) * mm});
            skLineSegment(sketch, "E197", {"start": v(2.33, -26.31) * mm, "end": v(2.33, -24.28) * mm});
            skLineSegment(sketch, "E198", {"start": v(-1.14, -24.28) * mm, "end": v(-1.14, -23.77) * mm});
            skLineSegment(sketch, "E199", {"start": v(-1.14, -26.31) * mm, "end": v(-1.14, -25.8) * mm});
            skLineSegment(sketch, "E200", {"start": v(-2.3, -24.28) * mm, "end": v(-2.3, -24.78) * mm});
            skLineSegment(sketch, "E201", {"start": v(-2.3, -25.3) * mm, "end": v(-2.3, -25.8) * mm});
            skLineSegment(sketch, "E202", {"start": v(-2.8, -23.77) * mm, "end": v(-2.8, -26.31) * mm});
            skLineSegment(sketch, "E203", {"start": v(-2.8, -23.77) * mm, "end": v(-1.14, -23.77) * mm});
            skLineSegment(sketch, "E204", {"start": v(-1.14, -26.31) * mm, "end": v(-2.8, -26.31) * mm});
            skLineSegment(sketch, "E205", {"start": v(-2.3, -24.28) * mm, "end": v(-1.14, -24.28) * mm});
            skLineSegment(sketch, "E206", {"start": v(-2.3, -25.8) * mm, "end": v(-1.14, -25.8) * mm});
            skLineSegment(sketch, "E207", {"start": v(-1.27, -24.78) * mm, "end": v(-1.27, -25.3) * mm});
            skLineSegment(sketch, "E208", {"start": v(-1.27, -25.3) * mm, "end": v(-2.3, -25.3) * mm});
            skLineSegment(sketch, "E209", {"start": v(-2.3, -24.78) * mm, "end": v(-1.27, -24.78) * mm});
            skSolve(sketch);
        }
        {
            var Q0;
            {var subQ1=sQuery(id+"F3.wireOp",EDGE,"E124");Q0=makeQuery(id+"F3.imprint","IMPRINT",FACE,{"disambiguationData":[TD([[makeQuery(id+"F3.imprint","IMPRINT",EDGE,{"derivedFrom":subQ1}),1.0]])]});}
            var Q1;
            {var subQ1=sQuery(id+"F3.wireOp",EDGE,"E123");Q1=makeQuery(id+"F3.imprint","IMPRINT",FACE,{"disambiguationData":[TD([[makeQuery(id+"F3.imprint","IMPRINT",EDGE,{"derivedFrom":subQ1}),1.0]])]});}
            var Q2;
            {var subQ4=sQuery(id+"F3.wireOp",EDGE,"E129");Q2=makeQuery(id+"F3.imprint","IMPRINT",FACE,{"disambiguationData":[TD([[makeQuery(id+"F3.imprint","IMPRINT",EDGE,{"derivedFrom":subQ4}),-1.0]])]});}
            var Q3;
            {var subQ3=sQuery(id+"F3.wireOp",EDGE,"E130");Q3=makeQuery(id+"F3.imprint","IMPRINT",FACE,{"disambiguationData":[TD([[makeQuery(id+"F3.imprint","IMPRINT",EDGE,{"derivedFrom":subQ3}),-1.0]])]});}
            var Q4;
            {var subQ1=sQuery(id+"F3.wireOp",EDGE,"E133");Q4=makeQuery(id+"F3.imprint","IMPRINT",FACE,{"disambiguationData":[TD([[makeQuery(id+"F3.imprint","IMPRINT",EDGE,{"derivedFrom":subQ1}),1.0]])]});}
            var Q5;
            {var subQ3=sQuery(id+"F3.wireOp",EDGE,"E135");Q5=makeQuery(id+"F3.imprint","IMPRINT",FACE,{"disambiguationData":[TD([[makeQuery(id+"F3.imprint","IMPRINT",EDGE,{"derivedFrom":subQ3}),-1.0]])]});}
            var Q6;
            {var subQ1=sQuery(id+"F3.wireOp",EDGE,"E137");Q6=makeQuery(id+"F3.imprint","IMPRINT",FACE,{"disambiguationData":[TD([[makeQuery(id+"F3.imprint","IMPRINT",EDGE,{"derivedFrom":subQ1}),1.0]])]});}
            var Q7;
            {var subQ3=sQuery(id+"F3.wireOp",EDGE,"E138");Q7=makeQuery(id+"F3.imprint","IMPRINT",FACE,{"disambiguationData":[TD([[makeQuery(id+"F3.imprint","IMPRINT",EDGE,{"derivedFrom":subQ3}),-1.0]])]});}
            var Q8;
            {var subQ7=sQuery(id+"F3.wireOp",EDGE,"E141");Q8=makeQuery(id+"F3.imprint","IMPRINT",FACE,{"disambiguationData":[TD([[makeQuery(id+"F3.imprint","IMPRINT",EDGE,{"derivedFrom":subQ7}),-1.0]])]});}
            var Q9;
            {var subQ4=sQuery(id+"F3.wireOp",EDGE,"E142");Q9=makeQuery(id+"F3.imprint","IMPRINT",FACE,{"disambiguationData":[TD([[makeQuery(id+"F3.imprint","IMPRINT",EDGE,{"derivedFrom":subQ4}),1.0]])]});}
            var Q10;
            {var subQ4=sQuery(id+"F3.wireOp",EDGE,"E145");Q10=makeQuery(id+"F3.imprint","IMPRINT",FACE,{"disambiguationData":[TD([[makeQuery(id+"F3.imprint","IMPRINT",EDGE,{"derivedFrom":subQ4}),1.0]])]});}
            var Q11;
            {var subQ3=sQuery(id+"F3.wireOp",EDGE,"E146");Q11=makeQuery(id+"F3.imprint","IMPRINT",FACE,{"disambiguationData":[TD([[makeQuery(id+"F3.imprint","IMPRINT",EDGE,{"derivedFrom":subQ3}),1.0]])]});}
            var Q12;
            Q12=makeQuery(id+"F3.imprint","IMPRINT",FACE,{"disambiguationData":[TD([[makeQuery(id+"F3.imprint","IMPRINT",EDGE,{"derivedFrom":sQuery(id+"F3.wireOp",EDGE,"E198")}),1.0]])]});
            var Q13;
            Q13=makeQuery(id+"F3.imprint","IMPRINT",FACE,{"disambiguationData":[TD([[makeQuery(id+"F3.imprint","IMPRINT",EDGE,{"derivedFrom":sQuery(id+"F3.wireOp",EDGE,"E177")}),1.0]])]});
            var Q14;
            Q14=makeQuery(id+"F3.imprint","IMPRINT",FACE,{"disambiguationData":[TD([[makeQuery(id+"F3.imprint","IMPRINT",EDGE,{"derivedFrom":sQuery(id+"F3.wireOp",EDGE,"E190")}),-1.0]])]});
            extrude(context, id + "F4", {"entities" : qUnion([Q0, Q1, Q2, Q3, Q4, Q5, Q6, Q7, Q8, Q9, Q10, Q11, Q12, Q13, Q14]), "depth" : 10.16 * mm, "offsetDistance" : 25.4 * mm});
        }
    });
